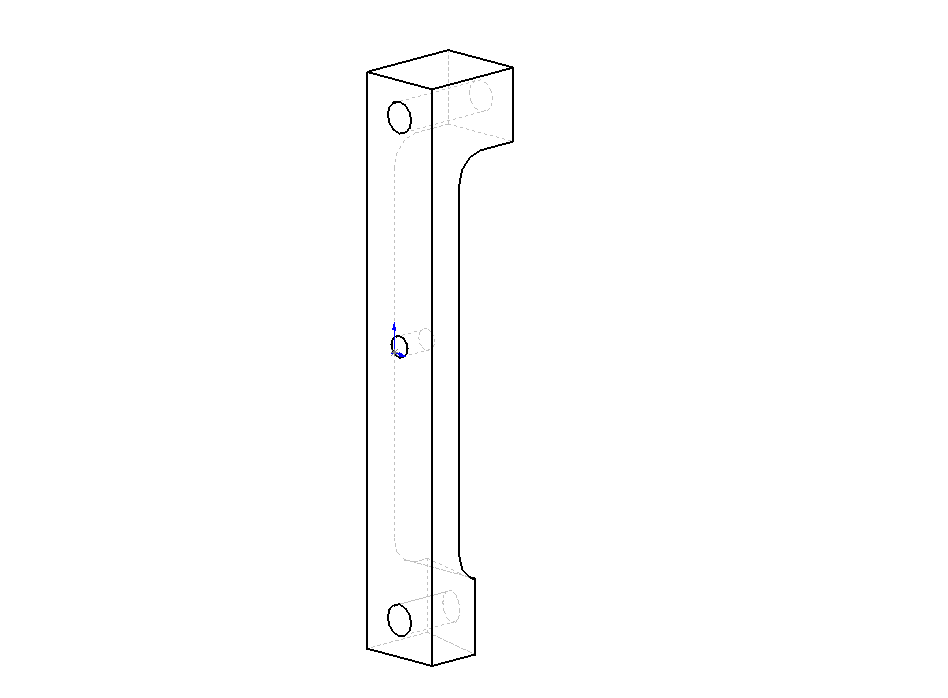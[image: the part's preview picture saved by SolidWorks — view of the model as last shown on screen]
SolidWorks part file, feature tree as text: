
SOLIDWORKS PART (.sldprt)
format: sldprt  version: not decoded by parser v0  size: 462,336 bytes
history: native  units: mm
features: sketch x6, extrude x2, cut_extrude x2, material x1, fillet x1, hole x1 + 1 further entry (+11 scaffold rows collapsed)
feature tree (25):
  scaffold x11  (default folders/planes/origin — collapsed)
  material  "Material <not specified>"
  "Origin"  ID=-1
  sketch  "Sketch1"  dims[D1=78.0mm D2=12.0mm D3=12.0mm D4=40.0mm]
  extrude  "Extrude1"  Depth=5mm
  sketch  "Sketch3"  dims[D1=2.9464mm D2=6.0mm D3=36.0mm]
  cut_extrude  "Cut-Extrude2"  [1 undecoded]
  sketch  "Sketch4"  dims[c1.D1=78.0mm c2.D1=90.0deg c3.D1=10.0mm c3.D2=10.0mm]
  extrude  "Extrude2"  Depth=10mm
  fillet  "Fillet1"  Radius=4mm
  sketch  "Sketch5"  dims[c1.D1=~12.465808mm c2.D1=15.0deg c3.D1=12.0mm c4.D1=15.0deg c5.D1=~12.833406mm c6.D1=15.2deg c6.D2=3.808mm]
  cut_extrude  "Cut-Extrude3"  [1 undecoded]
  hole  "#8 Clearance Hole1"  Diameter=4.3053mm Depth=15mm
  sketch  "3DSketch1"  dims[c1.D1=~68.343373mm c1.D4=67.5mm c1.D2=6.0mm c1.D3=5.0mm c2.D1=5.0mm]
  sketch  "Sketch7"  dims[hole-wizard template sketch: 60 standard entries collapsed; hole parameters kept: c18.Thru Hole Depth=15.0mm]
decode coverage: 10 of 12 modeling features carry decoded parameters; 1 rows unclassified (native names shown)
note: ~ marks probable driven/reference dimensions
note: 2 parameter values undecoded
note: suppression state not decoded; provenance and decode notes live in map.json
